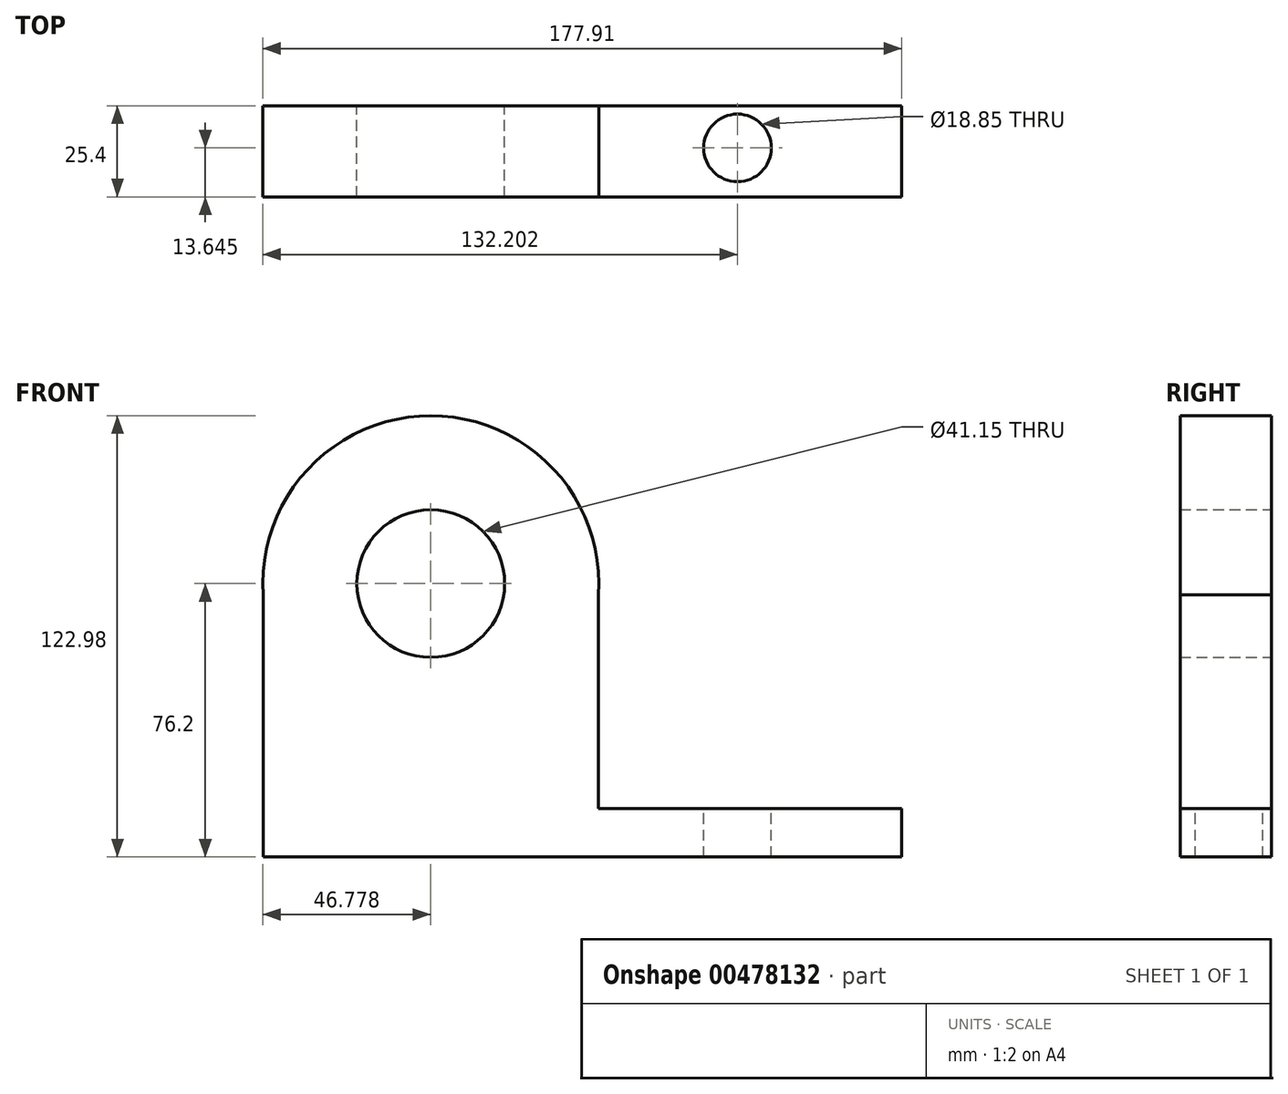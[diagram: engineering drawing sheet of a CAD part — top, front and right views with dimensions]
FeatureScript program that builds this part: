
annotation { "Feature Type Name" : "Feature", "Feature Type Description" : "" }
export const myFeature = defineFeature(function(context is Context, id is Id, definition is map)
    precondition{}
    {
        {
            var Q0;
            Q0=qCreatedBy(makeId("Front.planeOp"),FACE);
            var sketch = newSketch(context, id + "F0", { "sketchPlane" : qUnion([Q0])});
            skLineSegment(sketch, "E0", {"start": v(-93.34, 0) * mm, "end": v(84.46, 0) * mm});
            skLineSegment(sketch, "E1", {"start": v(-93.34, 0) * mm, "end": v(-93.34, 76.2) * mm});
            skLineSegment(sketch, "E2", {"start": v(-93.34, 76.2) * mm, "end": v(0, 76.2) * mm});
            skLineSegment(sketch, "E3", {"start": v(0, 76.2) * mm, "end": v(0, 0) * mm});
            skCircle(sketch, "E4", {"center": v(-46.67, 76.2) * mm, "radius": 46.78 * mm});
            skLineSegment(sketch, "E5", {"start": v(84.46, 0) * mm, "end": v(84.46, 13.5) * mm});
            skLineSegment(sketch, "E6", {"start": v(84.46, 13.5) * mm, "end": v(0, 13.5) * mm});
            skCircle(sketch, "E7", {"center": v(-46.67, 76.2) * mm, "radius": 20.57 * mm});
            skSolve(sketch);
        }
        {
            var Q0;
            {var subQ1=sQuery(id+"F0.wireOp",EDGE,"E2");var subQ7=sQuery(id+"F0.wireOp",EDGE,"E1");var subQ8=makeQuery(id+"F0.imprint","INTERSECT",VERTEX,{"derivedFrom":[subQ7,subQ1]});Q0=makeQuery(id+"F0.imprint","IMPRINT",FACE,{"disambiguationData":[TD([[makeQuery(id+"F0.imprint","IMPRINT",EDGE,{"disambiguationData":[TD([[subQ8,1.0]])],"derivedFrom":subQ7}),1.0]])]});}
            var Q1;
            {var subQ1=sQuery(id+"F0.wireOp",EDGE,"E2");var subQ7=sQuery(id+"F0.wireOp",EDGE,"E1");var subQ8=makeQuery(id+"F0.imprint","INTERSECT",VERTEX,{"derivedFrom":[subQ7,subQ1]});Q1=makeQuery(id+"F0.imprint","IMPRINT",FACE,{"disambiguationData":[TD([[makeQuery(id+"F0.imprint","IMPRINT",EDGE,{"disambiguationData":[TD([[subQ8,1.0]])],"derivedFrom":subQ7}),-1.0]])]});}
            var Q2;
            {var subQ1=sQuery(id+"F0.wireOp",EDGE,"E0");var subQ6=sQuery(id+"F0.wireOp",EDGE,"E1");var subQ7=makeQuery(id+"F0.imprint","INTERSECT",VERTEX,{"derivedFrom":[subQ1,subQ6]});Q2=makeQuery(id+"F0.imprint","IMPRINT",FACE,{"disambiguationData":[TD([[makeQuery(id+"F0.imprint","IMPRINT",EDGE,{"disambiguationData":[TD([[subQ7,-1.0]])],"derivedFrom":subQ1}),1.0]])]});}
            var Q3;
            {var subQ0=sQuery(id+"F0.wireOp",EDGE,"E5");Q3=makeQuery(id+"F0.imprint","IMPRINT",FACE,{"disambiguationData":[TD([[makeQuery(id+"F0.imprint","IMPRINT",EDGE,{"derivedFrom":subQ0}),1.0]])]});}
            extrude(context, id + "F1", {"entities" : qUnion([Q0, Q1, Q2, Q3]), "depth" : 25.4 * mm});
        }
        {
            var Q0;
            Q0=qCreatedBy(makeId("Top.planeOp"),FACE);
            var sketch = newSketch(context, id + "F2", { "sketchPlane" : qUnion([Q0])});
            skCircle(sketch, "E8", {"center": v(45.75, -12.04) * mm, "radius": 9.97 * mm});
            skSolve(sketch);
        }
        {
            var Q0;
            Q0 = qSketchRegion(id + "F2", true);
            extrude(context, id + "F3", {"entities" : qUnion([Q0]), "operationType" : NewBodyOperationType.REMOVE, "oppositeDirection" : true, "depth" : 25.4 * mm});
        }
        {
            var Q0;
            Q0=makeQuery(id+"F1.opExtrude","SWEPT_FACE",FACE,{"disambiguationData":[OSD([sQuery(id+"F0.wireOp",EDGE,"E6")])]});
            var sketch = newSketch(context, id + "F4", { "sketchPlane" : qUnion([Q0])});
            skCircle(sketch, "E9", {"center": v(38.75, -11.75) * mm, "radius": 9.42 * mm});
            skSolve(sketch);
        }
        {
            var Q0;
            Q0 = qSketchRegion(id + "F4", true);
            extrude(context, id + "F5", {"entities" : qUnion([Q0]), "operationType" : NewBodyOperationType.REMOVE, "oppositeDirection" : true, "depth" : 25.4 * mm});
        }
    });
